# Revit family: POR_Service_S5939_BIM_FR
name_source: partatom
category: Plumbing Fixtures
revit_build: Autodesk Revit 2017 (Build: 20160225_1515(x64)
units: mm (PartAtom-declared; Revit-internal decimal feet)

## family parameters
Cut with Voids When Loaded = Yes
Host = Face
OmniClass Number = 23.45.05.14.14.14
OmniClass Title = Clinic Sinks
Part Type = Normal
Room Calculation Point = No
Round Connector Dimension = Use Diameter
Shared = Yes

## types (1)
- S593901 - SERVICE POSTE EAU 46X38 AVEC GRILLE
    Accessoires = www.idealstandard.be
    Assembly Code = C1030200
    Auteur = Ideal Standard
    Bim-NomDuProjet = ISI_IdealStandard_CleanersSinks_S593901
    CWFU = 0
    Caractéristiques = Poste d'eau-service -S593901/ Porcher
    ConseilsDInstallation = www.idealstandard.be
    Cost = 0 $
    Couleur = Blanc
    CoûtDeRemplacement = 0
    DateDeCréation = 2018_08_15
    Default Elevation = 0 mm  [stored 0 ft]
    Description = SERVICE POSTE EAU 46X38 AVEC GRILLE
    DiamètreÉvacuation = 0
    Dimensions = 396 x 455 x 373 mm
    DuréeDeGarantieDesPièces = 2
    DuréeGarantie = ans
    DétailGarantie = Constructeur
    Espace = Interne
    Finition = Blanc
    Forme = Rectangulaire
    HWFU = 0
    Hauteur = 373 mm
    IfcExportAs = IfcSanitaryType
    IfcExportType = CLEANERSSINKS
    InformationsProduit = www.idealstandard.be
    Largeur = 455 mm  [stored 1.49278 ft]
    LienUtile = www.idealstandard.be
    Longueur = 395 mm
    Manufacturer = www.idealstandard.be
    Marque = PORCHER
    Matériel = Céramique
    Model = S593901
    Nom = CleanersSinks_S593901_IdealStandard
    PoidsNet = 36 kg
    Profondeur = 395 mm
    Raccordement = Plomberie
    Révision = 1
    TypeDImmobilisation = Fixe
    URL = www.idealstandard.be
    Uniclass2015Code = Pr_40_20_96_15
    Uniclass2015Title = Ceramic sinks
    Uniclass2015Version = Products v1.1
    UnitéDeTemps = an
    UrlDuFabricant = www.idealstandard.be
    Version = 1
    WFU = 0

note: [stored X ft] marks values corroborated as IEEE doubles in the binary element streams (Revit-internal decimal feet)

## geometry (parser evidence)
native form markers: Sweep x1
no freeform markers — native parametric forms only
